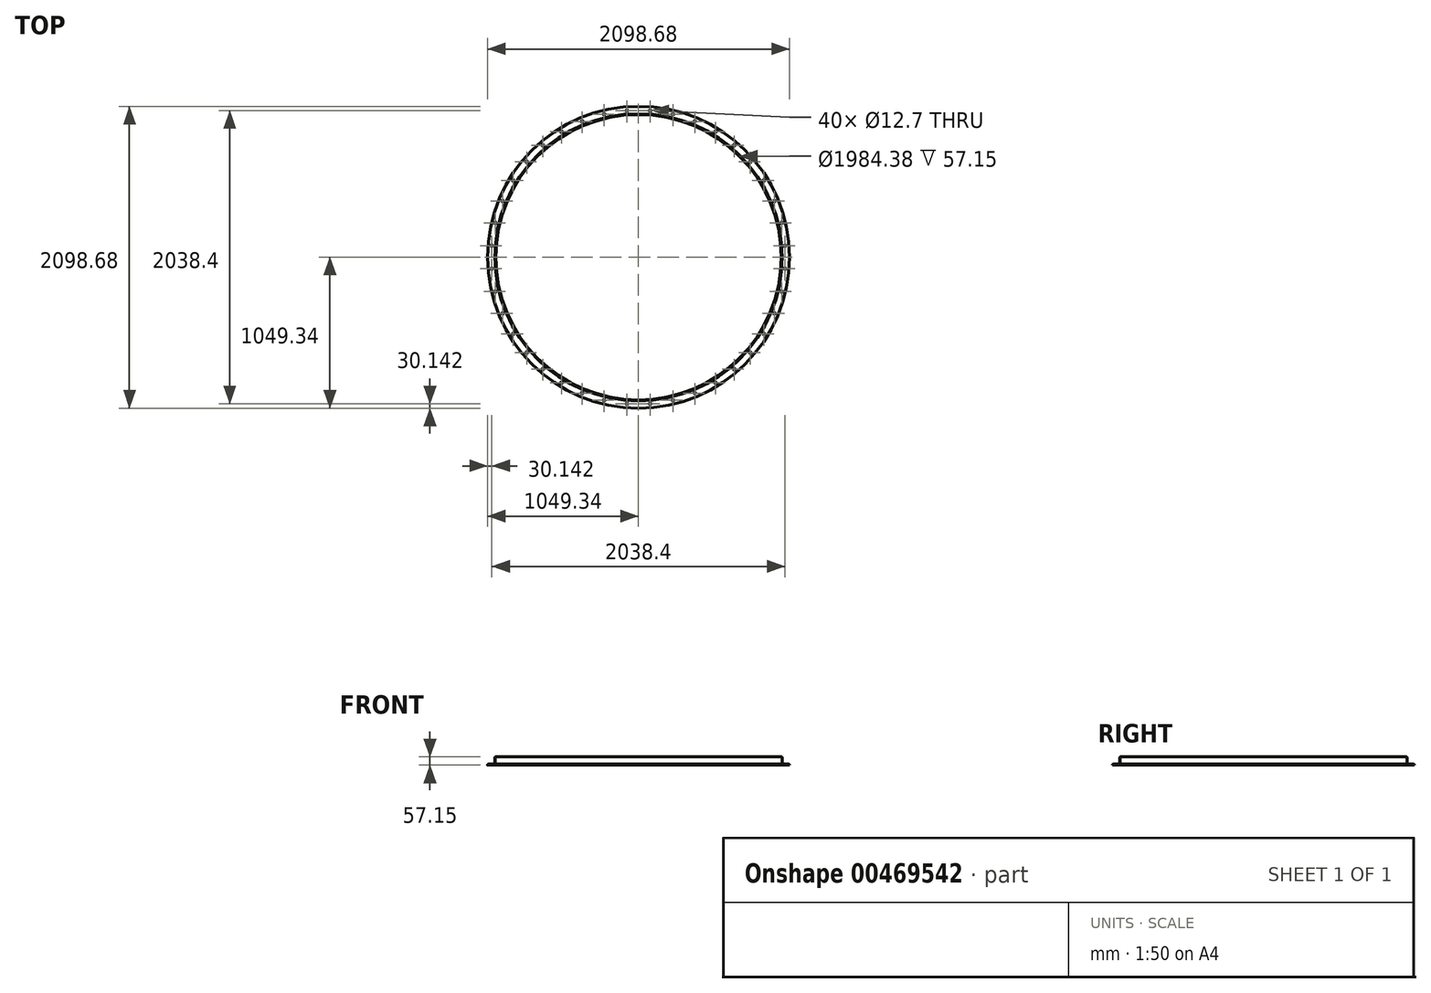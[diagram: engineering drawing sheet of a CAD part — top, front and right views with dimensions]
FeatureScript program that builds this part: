
annotation { "Feature Type Name" : "Feature", "Feature Type Description" : "" }
export const myFeature = defineFeature(function(context is Context, id is Id, definition is map)
    precondition{}
    {
        {
            var Q0;
            Q0=qCreatedBy(makeId("Front.planeOp"),FACE);
            var sketch = newSketch(context, id + "F0", { "sketchPlane" : qUnion([Q0])});
            skLineSegment(sketch, "E0", {"start": v(-1044.58, 0) * mm, "end": v(-1004.89, 0) * mm});
            skLineSegment(sketch, "E1", {"start": v(-998.54, 6.35) * mm, "end": v(-998.54, 46.04) * mm});
            skLineSegment(sketch, "E2", {"start": v(-992.19, 50.8) * mm, "end": v(-993.77, 50.8) * mm});
            skLineSegment(sketch, "E3", {"start": v(-1049.34, -6.35) * mm, "end": v(-1049.34, -4.76) * mm});
            skLineSegment(sketch, "E4", {"start": v(-1049.34, -6.35) * mm, "end": v(-992.19, -6.35) * mm});
            skLineSegment(sketch, "E5", {"start": v(-992.19, -6.35) * mm, "end": v(-992.19, 50.8) * mm});
            skPoint(sketch, "E6.visualSharp", {"position": v(-998.54, 50.8) * mm});
            skArc(sketch, "E6.filletArc", {"start": v(-993.77, 50.8) * mm, "mid": v(-997.14, 49.4) * mm, "end": v(-998.54, 46.04) * mm});
            skPoint(sketch, "E7.visualSharp", {"position": v(-1049.34, 0) * mm});
            skArc(sketch, "E7.filletArc", {"start": v(-1044.58, 0) * mm, "mid": v(-1047.94, -1.4) * mm, "end": v(-1049.34, -4.76) * mm});
            skPoint(sketch, "E8.visualSharp", {"position": v(-998.54, 0) * mm});
            skArc(sketch, "E8.filletArc", {"start": v(-1004.89, 0) * mm, "mid": v(-1000.4, 1.86) * mm, "end": v(-998.54, 6.35) * mm});
            skLineSegment(sketch, "E9", {"start": v(0, 0) * mm, "end": v(0, 50.8) * mm, "construction": true});
            skSolve(sketch);
        }
        {
            var Q0;
            Q0 = qSketchRegion(id + "F0", true);
            var Q1;
            Q1=sQuery(id+"F0.wireOp",EDGE,"E9");
            revolve(context, id + "F1", {"surfaceOperationType" : NewSurfaceOperationType.NEW, "entities" : qUnion([Q0]), "axis" : qUnion([Q1]), "revolveType" : RevolveType.FULL});
        }
        {
            var Q0;
            Q0=qCreatedBy(makeId("Top.planeOp"),FACE);
            var sketch = newSketch(context, id + "F2", { "sketchPlane" : qUnion([Q0])});
            skCircle(sketch, "E10", {"center": v(0, 0) * mm, "radius": 1022.35 * mm, "construction": true});
            skCircle(sketch, "E11", {"center": v(1019.2, 80.21) * mm, "radius": 6.35 * mm});
            skLineSegment(sketch, "E12", {"start": v(1019.2, 80.21) * mm, "end": v(0, 0) * mm, "construction": true});
            skCircle(sketch, "E13.1.0", {"center": v(994.1, 238.66) * mm, "radius": 6.35 * mm});
            skCircle(sketch, "E13.2.0", {"center": v(944.53, 391.24) * mm, "radius": 6.35 * mm});
            skCircle(sketch, "E13.3.0", {"center": v(871.7, 534.18) * mm, "radius": 6.35 * mm});
            skCircle(sketch, "E13.4.0", {"center": v(777.4, 663.96) * mm, "radius": 6.35 * mm});
            skCircle(sketch, "E13.5.0", {"center": v(663.96, 777.4) * mm, "radius": 6.35 * mm});
            skCircle(sketch, "E13.6.0", {"center": v(534.18, 871.7) * mm, "radius": 6.35 * mm});
            skCircle(sketch, "E13.7.0", {"center": v(391.24, 944.53) * mm, "radius": 6.35 * mm});
            skCircle(sketch, "E13.8.0", {"center": v(238.66, 994.1) * mm, "radius": 6.35 * mm});
            skCircle(sketch, "E13.9.0", {"center": v(80.21, 1019.2) * mm, "radius": 6.35 * mm});
            skCircle(sketch, "E13.10.0", {"center": v(-80.21, 1019.2) * mm, "radius": 6.35 * mm});
            skCircle(sketch, "E13.11.0", {"center": v(-238.66, 994.1) * mm, "radius": 6.35 * mm});
            skCircle(sketch, "E13.12.0", {"center": v(-391.24, 944.53) * mm, "radius": 6.35 * mm});
            skCircle(sketch, "E13.13.0", {"center": v(-534.18, 871.7) * mm, "radius": 6.35 * mm});
            skCircle(sketch, "E13.14.0", {"center": v(-663.96, 777.4) * mm, "radius": 6.35 * mm});
            skCircle(sketch, "E13.15.0", {"center": v(-777.4, 663.96) * mm, "radius": 6.35 * mm});
            skCircle(sketch, "E13.16.0", {"center": v(-871.7, 534.18) * mm, "radius": 6.35 * mm});
            skCircle(sketch, "E13.17.0", {"center": v(-944.53, 391.24) * mm, "radius": 6.35 * mm});
            skCircle(sketch, "E13.18.0", {"center": v(-994.1, 238.66) * mm, "radius": 6.35 * mm});
            skCircle(sketch, "E13.19.0", {"center": v(-1019.2, 80.21) * mm, "radius": 6.35 * mm});
            skCircle(sketch, "E13.20.0", {"center": v(-1019.2, -80.21) * mm, "radius": 6.35 * mm});
            skCircle(sketch, "E13.21.0", {"center": v(-994.1, -238.66) * mm, "radius": 6.35 * mm});
            skCircle(sketch, "E13.22.0", {"center": v(-944.53, -391.24) * mm, "radius": 6.35 * mm});
            skCircle(sketch, "E13.23.0", {"center": v(-871.7, -534.18) * mm, "radius": 6.35 * mm});
            skCircle(sketch, "E13.24.0", {"center": v(-777.4, -663.96) * mm, "radius": 6.35 * mm});
            skCircle(sketch, "E13.25.0", {"center": v(-663.96, -777.4) * mm, "radius": 6.35 * mm});
            skCircle(sketch, "E13.26.0", {"center": v(-534.18, -871.7) * mm, "radius": 6.35 * mm});
            skCircle(sketch, "E13.27.0", {"center": v(-391.24, -944.53) * mm, "radius": 6.35 * mm});
            skCircle(sketch, "E13.28.0", {"center": v(-238.66, -994.1) * mm, "radius": 6.35 * mm});
            skCircle(sketch, "E13.29.0", {"center": v(-80.21, -1019.2) * mm, "radius": 6.35 * mm});
            skCircle(sketch, "E13.30.0", {"center": v(80.21, -1019.2) * mm, "radius": 6.35 * mm});
            skCircle(sketch, "E13.31.0", {"center": v(238.66, -994.1) * mm, "radius": 6.35 * mm});
            skCircle(sketch, "E13.32.0", {"center": v(391.24, -944.53) * mm, "radius": 6.35 * mm});
            skCircle(sketch, "E13.33.0", {"center": v(534.18, -871.7) * mm, "radius": 6.35 * mm});
            skCircle(sketch, "E13.34.0", {"center": v(663.96, -777.4) * mm, "radius": 6.35 * mm});
            skCircle(sketch, "E13.35.0", {"center": v(777.4, -663.96) * mm, "radius": 6.35 * mm});
            skCircle(sketch, "E13.36.0", {"center": v(871.7, -534.18) * mm, "radius": 6.35 * mm});
            skCircle(sketch, "E13.37.0", {"center": v(944.53, -391.24) * mm, "radius": 6.35 * mm});
            skCircle(sketch, "E13.38.0", {"center": v(994.1, -238.66) * mm, "radius": 6.35 * mm});
            skCircle(sketch, "E13.39.0", {"center": v(1019.2, -80.21) * mm, "radius": 6.35 * mm});
            skLineSegment(sketch, "E14", {"start": v(0, 0) * mm, "end": v(1019.2, -80.21) * mm, "construction": true});
            skSolve(sketch);
        }
        {
            var Q0;
            Q0 = qSketchRegion(id + "F2", true);
            extrude(context, id + "F3", {"entities" : qUnion([Q0]), "operationType" : NewBodyOperationType.REMOVE, "endBound" : BoundingType.THROUGH_ALL, "oppositeDirection" : true, "depth" : 25.4 * mm, "offsetDistance" : 25.4 * mm});
        }
    });
